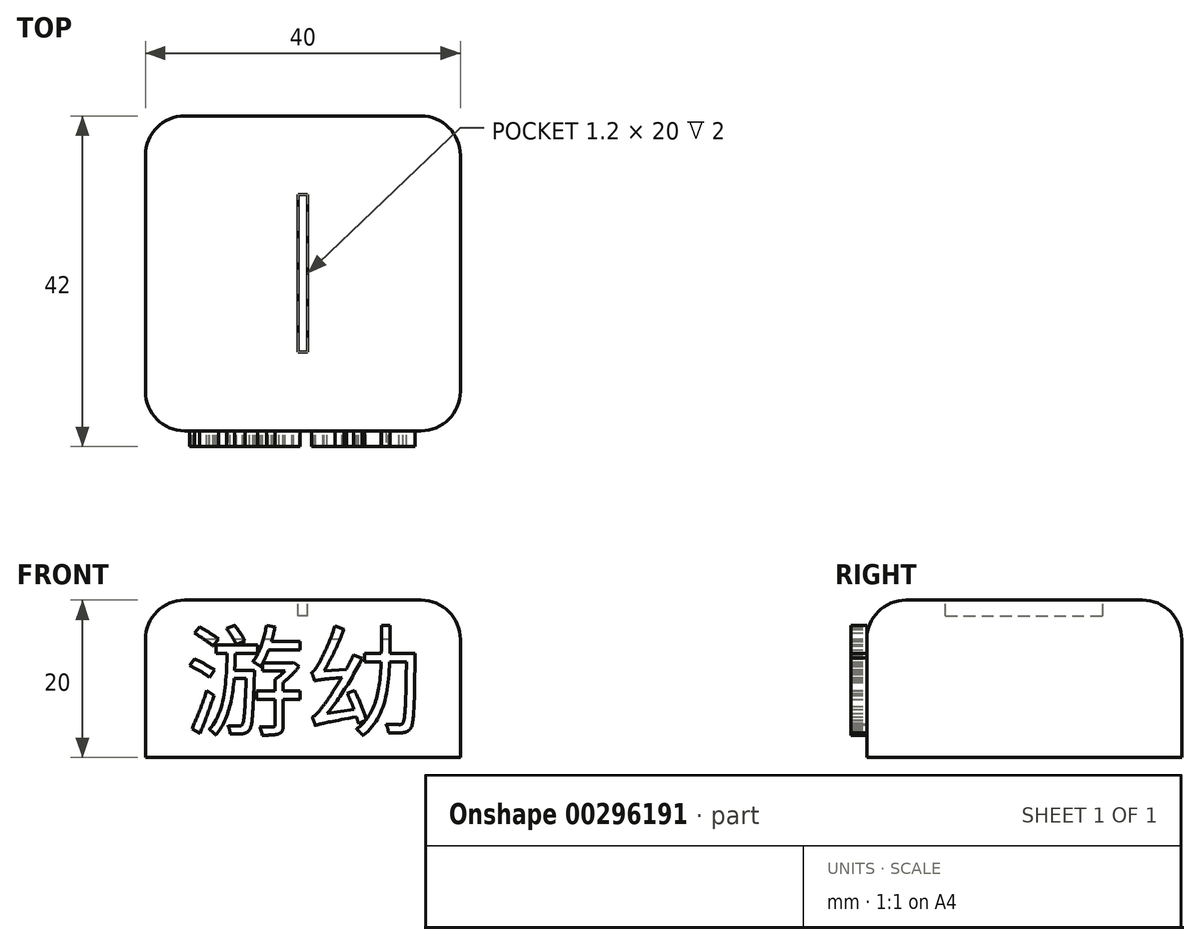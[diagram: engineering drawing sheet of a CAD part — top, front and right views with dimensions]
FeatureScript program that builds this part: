
annotation { "Feature Type Name" : "Feature", "Feature Type Description" : "" }
export const myFeature = defineFeature(function(context is Context, id is Id, definition is map)
    precondition{}
    {
        {
            var Q0;
            Q0=qCreatedBy(makeId("Top.planeOp"),FACE);
            var sketch = newSketch(context, id + "F0", { "sketchPlane" : qUnion([Q0])});
            skLineSegment(sketch, "E0.bottom", {"start": v(20, -20) * mm, "end": v(-20, -20) * mm});
            skLineSegment(sketch, "E0.top", {"start": v(20, 20) * mm, "end": v(-20, 20) * mm});
            skLineSegment(sketch, "E0.left", {"start": v(20, -20) * mm, "end": v(20, 20) * mm});
            skLineSegment(sketch, "E0.right", {"start": v(-20, -20) * mm, "end": v(-20, 20) * mm});
            skPoint(sketch, "E0.middle", {"position": v(0, 0) * mm});
            skLineSegment(sketch, "E1.bottom", {"start": v(0.6, -10) * mm, "end": v(-0.6, -10) * mm});
            skLineSegment(sketch, "E1.top", {"start": v(0.6, 10) * mm, "end": v(-0.6, 10) * mm});
            skLineSegment(sketch, "E1.left", {"start": v(0.6, -10) * mm, "end": v(0.6, 10) * mm});
            skLineSegment(sketch, "E1.right", {"start": v(-0.6, -10) * mm, "end": v(-0.6, 10) * mm});
            skSolve(sketch);
        }
        {
            var Q0;
            Q0=makeQuery(id+"F0.imprint","IMPRINT",FACE,{"disambiguationData":[TD([[makeQuery(id+"F0.imprint","IMPRINT",EDGE,{"derivedFrom":sQuery(id+"F0.wireOp",EDGE,"E0.bottom")}),-1.0]])]});
            var Q1;
            Q1=makeQuery(id+"F0.imprint","IMPRINT",FACE,{"disambiguationData":[TD([[makeQuery(id+"F0.imprint","IMPRINT",EDGE,{"derivedFrom":sQuery(id+"F0.wireOp",EDGE,"E1.bottom")}),-1.0]])]});
            extrude(context, id + "F1", {"entities" : qUnion([Q0, Q1]), "oppositeDirection" : true, "depth" : 20 * mm});
        }
        {
            var Q0;
            Q0=makeQuery(id+"F0.imprint","IMPRINT",FACE,{"disambiguationData":[TD([[makeQuery(id+"F0.imprint","IMPRINT",EDGE,{"derivedFrom":sQuery(id+"F0.wireOp",EDGE,"E1.bottom")}),-1.0]])]});
            extrude(context, id + "F2", {"entities" : qUnion([Q0]), "operationType" : NewBodyOperationType.REMOVE, "oppositeDirection" : true, "depth" : 2 * mm});
        }
        {
            var Q0;
            Q0=makeQuery(id+"F2.boolean.opBoolean","COPY",EDGE,{"derivedFrom":makeQuery(id+"F2.opExtrude","CAP_EDGE",EDGE,{"disambiguationData":[OSD([sQuery(id+"F0.wireOp",EDGE,"E1.left")])],"isStart":true})});
            var Q1;
            Q1=makeQuery(id+"F2.boolean.opBoolean","COPY",EDGE,{"derivedFrom":makeQuery(id+"F2.opExtrude","CAP_EDGE",EDGE,{"disambiguationData":[OSD([sQuery(id+"F0.wireOp",EDGE,"E1.right")])],"isStart":true})});
            var Q2;
            Q2=makeQuery(id+"F1.opExtrude","SWEPT_EDGE",EDGE,{"disambiguationData":[OSD([sQuery(id+"F0.wireOp",EDGE,"E0.bottom"),sQuery(id+"F0.wireOp",EDGE,"E0.left")])]});
            var Q3;
            Q3=makeQuery(id+"F1.opExtrude","SWEPT_EDGE",EDGE,{"disambiguationData":[OSD([sQuery(id+"F0.wireOp",EDGE,"E0.top"),sQuery(id+"F0.wireOp",EDGE,"E0.left")])]});
            var Q4;
            Q4=makeQuery(id+"F1.opExtrude","CAP_EDGE",EDGE,{"disambiguationData":[OSD([sQuery(id+"F0.wireOp",EDGE,"E0.left")])],"isStart":true});
            var Q5;
            Q5=makeQuery(id+"F1.opExtrude","SWEPT_EDGE",EDGE,{"disambiguationData":[OSD([sQuery(id+"F0.wireOp",EDGE,"E0.bottom"),sQuery(id+"F0.wireOp",EDGE,"E0.right")])]});
            var Q6;
            Q6=makeQuery(id+"F1.opExtrude","SWEPT_EDGE",EDGE,{"disambiguationData":[OSD([sQuery(id+"F0.wireOp",EDGE,"E0.top"),sQuery(id+"F0.wireOp",EDGE,"E0.right")])]});
            var Q7;
            Q7=makeQuery(id+"F1.opExtrude","CAP_EDGE",EDGE,{"disambiguationData":[OSD([sQuery(id+"F0.wireOp",EDGE,"E0.top")])],"isStart":true});
            var Q8;
            Q8=makeQuery(id+"F1.opExtrude","CAP_EDGE",EDGE,{"disambiguationData":[OSD([sQuery(id+"F0.wireOp",EDGE,"E0.right")])],"isStart":true});
            var Q9;
            Q9=makeQuery(id+"F1.opExtrude","CAP_EDGE",EDGE,{"disambiguationData":[OSD([sQuery(id+"F0.wireOp",EDGE,"E0.bottom")])],"isStart":true});
            fillet(context, id + "F3", {"entities" : qUnion([Q0, Q1, Q2, Q3, Q4, Q5, Q6, Q7, Q8, Q9]), "radius" : 5 * mm, "tangentPropagation" : true, "allowEdgeOverflow" : false});
        }
        {
            var Q0;
            Q0=makeQuery(id+"F1.opExtrude","SWEPT_FACE",FACE,{"disambiguationData":[OSD([sQuery(id+"F0.wireOp",EDGE,"E0.bottom")])]});
            var sketch = newSketch(context, id + "F4", { "sketchPlane" : qUnion([Q0])});
            skText(sketch, "E2", { "text": "游幼", "fontName": "NotoSansCJKtc-Regular.otf"});
            const initialGuessF4  = {"E2": [-0.015, -0.01599, 1, 0, 0.01099]};
            skSetInitialGuess(sketch, initialGuessF4);
            skSolve(sketch);
        }
        {
            var Q0;
            Q0 = qSketchRegion(id + "F4", true);
            extrude(context, id + "F5", {"entities" : qUnion([Q0]), "operationType" : NewBodyOperationType.ADD, "depth" : 2 * mm});
        }
    });
